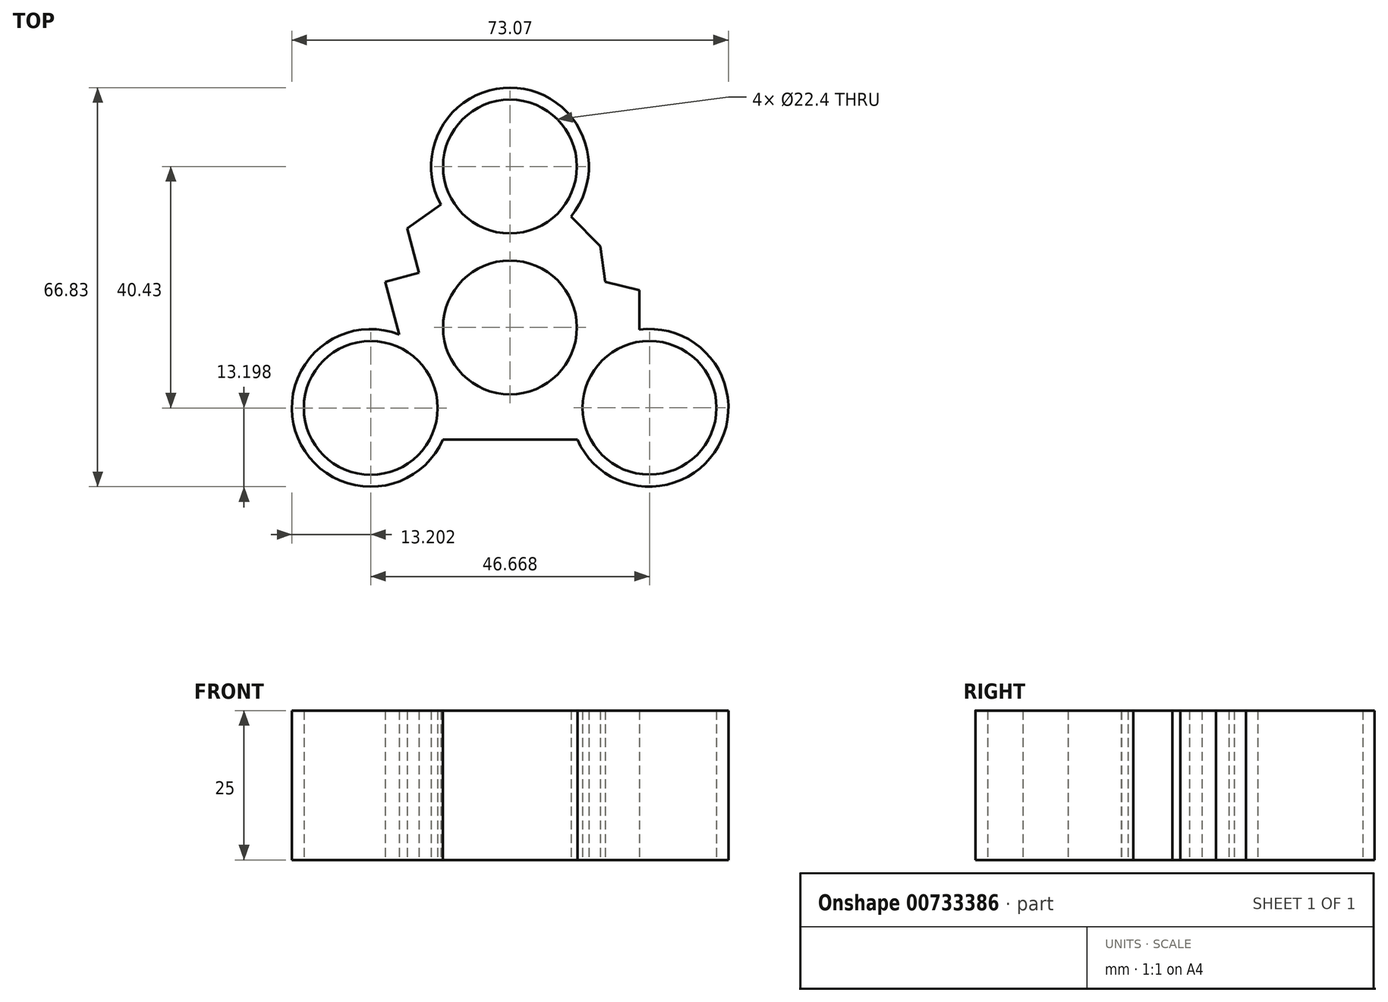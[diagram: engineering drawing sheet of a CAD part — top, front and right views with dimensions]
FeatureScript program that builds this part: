
annotation { "Feature Type Name" : "Feature", "Feature Type Description" : "" }
export const myFeature = defineFeature(function(context is Context, id is Id, definition is map)
    precondition{}
    {
        {
            var Q0;
            Q0=qCreatedBy(makeId("Top.planeOp"),FACE);
            var sketch = newSketch(context, id + "F0", { "sketchPlane" : qUnion([Q0])});
            skCircle(sketch, "E0", {"center": v(0, 0) * mm, "radius": 11.2 * mm});
            skCircle(sketch, "E1", {"center": v(0, 26.95) * mm, "radius": 11.2 * mm});
            skArc(sketch, "E2", {"start": v(10.2, 18.58) * mm, "mid": v(1.2, 40.1) * mm, "end": v(-11.56, 20.57) * mm});
            skArc(sketch, "E3.1.0", {"start": v(-18.53, -1.18) * mm, "mid": v(-35.5, -18.55) * mm, "end": v(-11.21, -18.77) * mm});
            skCircle(sketch, "E3.1.1", {"center": v(-23.3, -13.48) * mm, "radius": 11.2 * mm});
            skArc(sketch, "E3.2.0", {"start": v(11.28, -18.77) * mm, "mid": v(34.85, -19.94) * mm, "end": v(21.66, -0.36) * mm});
            skCircle(sketch, "E3.2.1", {"center": v(23.36, -13.45) * mm, "radius": 11.2 * mm});
            skPoint(sketch, "E3.center", {"position": v(0.02, 0) * mm});
            skLineSegment(sketch, "E4", {"start": v(-11.56, 20.57) * mm, "end": v(-17.18, 16.62) * mm});
            skLineSegment(sketch, "E5", {"start": v(-17.18, 16.62) * mm, "end": v(-15.25, 9.16) * mm});
            skLineSegment(sketch, "E6", {"start": v(-15.25, 9.16) * mm, "end": v(-20.9, 7.64) * mm});
            skLineSegment(sketch, "E7", {"start": v(-20.9, 7.64) * mm, "end": v(-18.53, -1.18) * mm});
            skLineSegment(sketch, "E8", {"start": v(10.2, 18.58) * mm, "end": v(15.15, 13.6) * mm});
            skLineSegment(sketch, "E9", {"start": v(15.15, 13.6) * mm, "end": v(15.96, 7.64) * mm});
            skLineSegment(sketch, "E10", {"start": v(15.96, 7.64) * mm, "end": v(21.66, 6.25) * mm});
            skLineSegment(sketch, "E11", {"start": v(21.66, 6.25) * mm, "end": v(21.66, -0.36) * mm});
            skLineSegment(sketch, "E12", {"start": v(-11.21, -18.77) * mm, "end": v(11.28, -18.77) * mm});
            skLineSegment(sketch, "E13", {"start": v(-11.56, 20.57) * mm, "end": v(-5.57, 9.72) * mm});
            skLineSegment(sketch, "E14", {"start": v(12.68, 16.09) * mm, "end": v(10.2, 18.58) * mm});
            skLineSegment(sketch, "E15", {"start": v(11.26, 17.88) * mm, "end": v(3.83, 10.52) * mm});
            skLineSegment(sketch, "E16", {"start": v(0, -11.2) * mm, "end": v(1.96, -18.77) * mm});
            skLineSegment(sketch, "E17", {"start": v(1.96, -18.77) * mm, "end": v(0, -18.18) * mm});
            skSolve(sketch);
        }
        {
            var Q0;
            Q0 = qSketchRegion(id + "F0", true);
            extrude(context, id + "F1", {"entities" : qUnion([Q0]), "depth" : 25 * mm, "offsetDistance" : 25 * mm});
        }
    });
